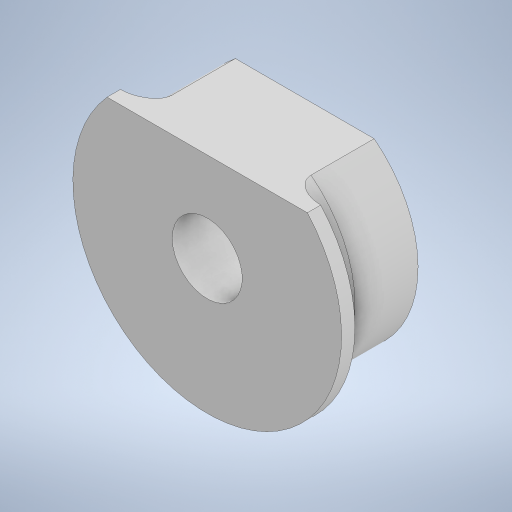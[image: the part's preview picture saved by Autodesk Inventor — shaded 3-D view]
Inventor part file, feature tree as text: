
AUTODESK INVENTOR PART (.ipt)
format: ipt  version: 2023 (Build 270158000, 158)  size: 251,904 bytes
history: native  units: in
note: dims shown in document units (in); Inventor stores cm internally (conversion verified against a paired STEP export)
features: sketch x2, revolve x1, extrude x1
ambient origin geometry x8: Origin, YZ Plane, XZ Plane, XY Plane, X Axis, Y Axis, Z Axis, Center Point
bodies: Solid1 (feature_tree)
feature tree (4):
  revolve  "Revolution1"  [1 undecoded]
  extrude  "Extrusion1"  [1 undecoded]
  sketch  "Sketch1"  dims[d5=360.0deg d9=0.1in]
  sketch  "Sketch2"  dims[d10=1.0in d11=0.0in]
note: 2 required parameter values undecoded (feature->parameter linkage not recoverable at this tier; creation-order binding heuristic only, values carry confidence <= 0.55)